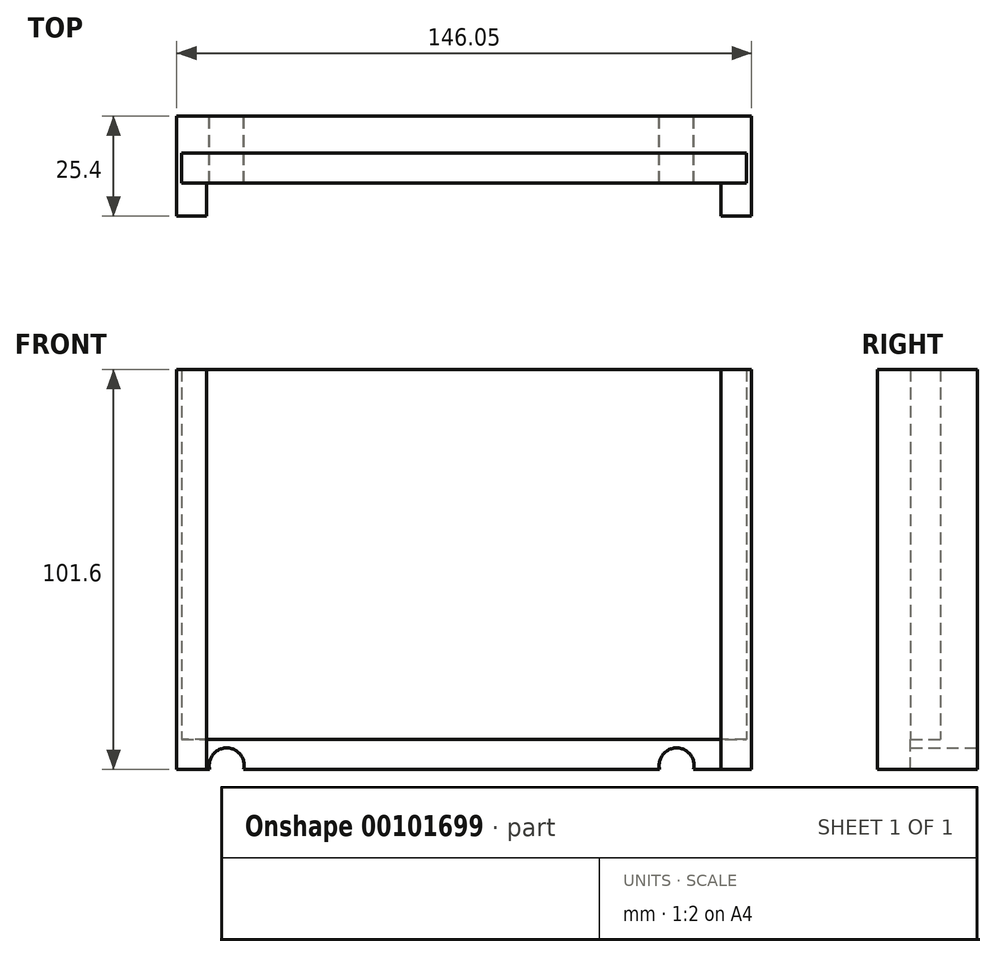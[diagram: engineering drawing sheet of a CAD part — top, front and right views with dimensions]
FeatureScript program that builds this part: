
annotation { "Feature Type Name" : "Feature", "Feature Type Description" : "" }
export const myFeature = defineFeature(function(context is Context, id is Id, definition is map)
    precondition{}
    {
        {
            var Q0;
            Q0=qCreatedBy(makeId("Top.planeOp"),FACE);
            var sketch = newSketch(context, id + "F0", { "sketchPlane" : qUnion([Q0])});
            skLineSegment(sketch, "E0.bottom", {"start": v(-68.8, -4.9) * mm, "end": v(77.24, -4.9) * mm});
            skLineSegment(sketch, "E0.top", {"start": v(-68.8, -30.3) * mm, "end": v(77.24, -30.3) * mm});
            skLineSegment(sketch, "E0.left", {"start": v(-68.8, -4.9) * mm, "end": v(-68.8, -30.3) * mm});
            skLineSegment(sketch, "E0.right", {"start": v(77.24, -4.9) * mm, "end": v(77.24, -30.3) * mm});
            skSolve(sketch);
        }
        {
            var Q0;
            Q0 = qSketchRegion(id + "F0", true);
            extrude(context, id + "F1", {"entities" : qUnion([Q0]), "depth" : 101.6 * mm});
        }
        {
            var Q0;
            Q0=makeQuery(id+"F1.opExtrude","CAP_FACE",FACE,{"disambiguationData":[OSD([sQuery(id+"F0.wireOp",EDGE,"E0.bottom"),sQuery(id+"F0.wireOp",EDGE,"E0.top"),sQuery(id+"F0.wireOp",EDGE,"E0.left"),sQuery(id+"F0.wireOp",EDGE,"E0.right")])],"isStart":false});
            var sketch = newSketch(context, id + "F2", { "sketchPlane" : qUnion([Q0])});
            skLineSegment(sketch, "E1", {"start": v(-63.3, -14.3) * mm, "end": v(-68.8, -14.3) * mm});
            skLineSegment(sketch, "E2", {"start": v(-63.3, -14.3) * mm, "end": v(77.24, -14.3) * mm});
            skLineSegment(sketch, "E3", {"start": v(-63.3, -21.92) * mm, "end": v(-68.8, -21.92) * mm});
            skLineSegment(sketch, "E4", {"start": v(-63.3, -21.92) * mm, "end": v(77.24, -21.92) * mm});
            skLineSegment(sketch, "E5", {"start": v(77.24, -21.92) * mm, "end": v(77.24, -14.3) * mm});
            skLineSegment(sketch, "E6", {"start": v(-68.8, -21.92) * mm, "end": v(-68.8, -14.3) * mm});
            skSolve(sketch);
        }
        {
            var Q0;
            Q0 = qSketchRegion(id + "F2", true);
            extrude(context, id + "F3", {"entities" : qUnion([Q0]), "operationType" : NewBodyOperationType.REMOVE, "oppositeDirection" : true, "depth" : 93.98 * mm});
        }
        {
            var Q0;
            {var subQ0=sQuery(id+"F0.wireOp",EDGE,"E0.top");var subQ1=sQuery(id+"F0.wireOp",EDGE,"E0.left");var subQ2=sQuery(id+"F0.wireOp",EDGE,"E0.right");Q0=makeQuery(id+"F3.boolean.opBoolean","SPLIT",FACE,{"disambiguationData":[TD([makeQuery(id+"F1.opExtrude","SWEPT_FACE",FACE,{"disambiguationData":[OSD([subQ0])]})])],"derivedFrom":makeQuery(id+"F1.opExtrude","CAP_FACE",FACE,{"disambiguationData":[OSD([sQuery(id+"F0.wireOp",EDGE,"E0.bottom"),subQ0,subQ1,subQ2])],"isStart":false})});}
            var sketch = newSketch(context, id + "F4", { "sketchPlane" : qUnion([Q0])});
            skLineSegment(sketch, "E7", {"start": v(-61.19, -26.11) * mm, "end": v(-61.19, -30.3) * mm});
            skLineSegment(sketch, "E8", {"start": v(-61.19, -30.3) * mm, "end": v(-61.19, -21.92) * mm});
            skLineSegment(sketch, "E9", {"start": v(69.41, -26.11) * mm, "end": v(69.41, -21.92) * mm});
            skLineSegment(sketch, "E10", {"start": v(69.41, -21.92) * mm, "end": v(69.41, -30.3) * mm});
            skLineSegment(sketch, "E11", {"start": v(69.41, -30.3) * mm, "end": v(-61.19, -30.3) * mm});
            skLineSegment(sketch, "E12", {"start": v(-61.19, -21.92) * mm, "end": v(69.41, -21.92) * mm});
            skSolve(sketch);
        }
        {
            var Q0;
            Q0 = qSketchRegion(id + "F4", true);
            extrude(context, id + "F5", {"entities" : qUnion([Q0]), "operationType" : NewBodyOperationType.REMOVE, "endBound" : BoundingType.THROUGH_ALL, "oppositeDirection" : true, "depth" : 25.4 * mm});
        }
        {
            var Q0;
            Q0=makeQuery(id+"F1.opExtrude","SWEPT_FACE",FACE,{"disambiguationData":[OSD([sQuery(id+"F0.wireOp",EDGE,"E0.bottom")])]});
            var sketch = newSketch(context, id + "F6", { "sketchPlane" : qUnion([Q0])});
            skCircle(sketch, "E13", {"center": v(-58.2, 1.02) * mm, "radius": 4.45 * mm});
            skCircle(sketch, "E14", {"center": v(56.1, 1.02) * mm, "radius": 4.45 * mm});
            skSolve(sketch);
        }
        {
            var Q0;
            Q0 = qSketchRegion(id + "F6", true);
            extrude(context, id + "F7", {"entities" : qUnion([Q0]), "operationType" : NewBodyOperationType.REMOVE, "endBound" : BoundingType.THROUGH_ALL, "oppositeDirection" : true, "depth" : 25.4 * mm});
        }
        {
            var Q0;
            Q0=makeQuery(id+"F3.boolean.opBoolean","COPY",FACE,{"derivedFrom":makeQuery(id+"F3.opExtrude","SWEPT_FACE",FACE,{"disambiguationData":[OSD([sQuery(id+"F2.wireOp",EDGE,"E1"),sQuery(id+"F2.wireOp",EDGE,"E2")])]})});
            var sketch = newSketch(context, id + "F8", { "sketchPlane" : qUnion([Q0])});
            skLineSegment(sketch, "E15.bottom", {"start": v(75.97, 101.6) * mm, "end": v(77.24, 101.6) * mm});
            skLineSegment(sketch, "E15.top", {"start": v(75.97, 7.62) * mm, "end": v(77.24, 7.62) * mm});
            skLineSegment(sketch, "E15.left", {"start": v(75.97, 101.6) * mm, "end": v(75.97, 7.62) * mm});
            skLineSegment(sketch, "E15.right", {"start": v(77.24, 101.6) * mm, "end": v(77.24, 7.62) * mm});
            skLineSegment(sketch, "E16.bottom", {"start": v(-68.8, 101.6) * mm, "end": v(-67.54, 101.6) * mm});
            skLineSegment(sketch, "E16.top", {"start": v(-68.8, 7.62) * mm, "end": v(-67.54, 7.62) * mm});
            skLineSegment(sketch, "E16.left", {"start": v(-68.8, 101.6) * mm, "end": v(-68.8, 7.62) * mm});
            skLineSegment(sketch, "E16.right", {"start": v(-67.54, 101.6) * mm, "end": v(-67.54, 7.62) * mm});
            skSolve(sketch);
        }
        {
            var Q0;
            Q0 = qSketchRegion(id + "F8", true);
            extrude(context, id + "F9", {"entities" : qUnion([Q0]), "operationType" : NewBodyOperationType.ADD, "depth" : 7.62 * mm});
        }
    });
